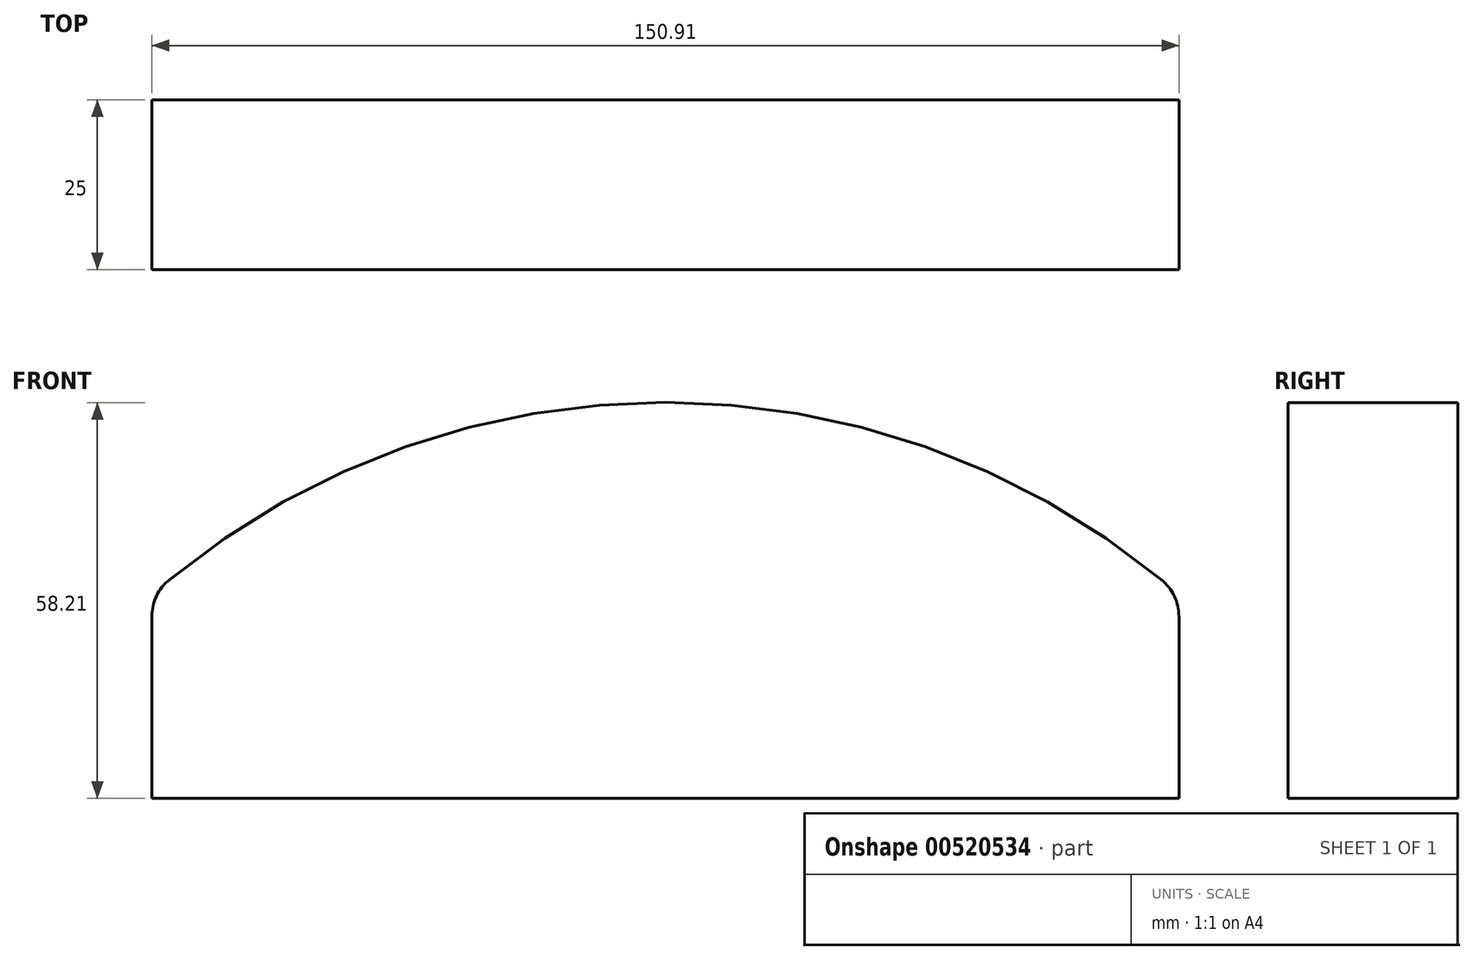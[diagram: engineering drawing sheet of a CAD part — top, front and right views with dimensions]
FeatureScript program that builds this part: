
annotation { "Feature Type Name" : "Feature", "Feature Type Description" : "" }
export const myFeature = defineFeature(function(context is Context, id is Id, definition is map)
    precondition{}
    {
        {
            var Q0;
            Q0=qCreatedBy(makeId("Front.planeOp"),FACE);
            var sketch = newSketch(context, id + "F0", { "sketchPlane" : qUnion([Q0])});
            skArc(sketch, "E0", {"start": v(71.65, 2.16) * mm, "mid": v(-1.25, 28.21) * mm, "end": v(-74.14, 2.16) * mm});
            skLineSegment(sketch, "E1", {"start": v(-76.7, -3.25) * mm, "end": v(-76.7, -30) * mm});
            skLineSegment(sketch, "E2", {"start": v(74.2, -3.25) * mm, "end": v(74.2, -30) * mm});
            skPoint(sketch, "E3.visualSharp", {"position": v(-76.7, 0) * mm});
            skArc(sketch, "E3.filletArc", {"start": v(-74.14, 2.16) * mm, "mid": v(-76.03, -0.26) * mm, "end": v(-76.7, -3.25) * mm});
            skPoint(sketch, "E4.visualSharp", {"position": v(74.2, 0) * mm});
            skArc(sketch, "E4.filletArc", {"start": v(74.2, -3.25) * mm, "mid": v(73.54, -0.26) * mm, "end": v(71.65, 2.16) * mm});
            skLineSegment(sketch, "E5", {"start": v(-76.7, -30) * mm, "end": v(74.2, -30) * mm});
            skSolve(sketch);
        }
        {
            var Q0;
            Q0=makeQuery(id+"F0.imprint","IMPRINT",FACE,{"disambiguationData":[TD([[makeQuery(id+"F0.imprint","IMPRINT",EDGE,{"derivedFrom":sQuery(id+"F0.wireOp",EDGE,"E0")}),1.0]])]});
            extrude(context, id + "F1", {"entities" : qUnion([Q0]), "depth" : 25 * mm, "offsetDistance" : 25 * mm});
        }
    });
